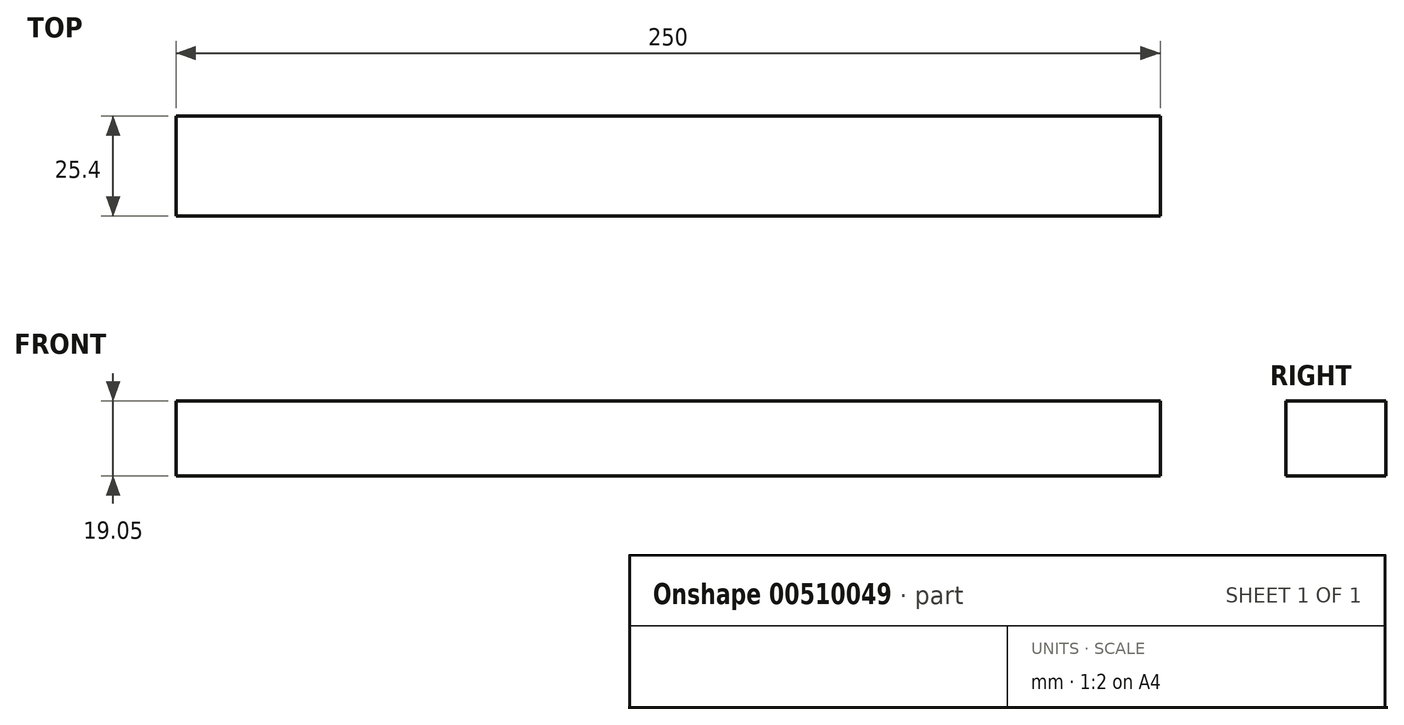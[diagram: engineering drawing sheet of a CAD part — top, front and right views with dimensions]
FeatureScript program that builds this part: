
annotation { "Feature Type Name" : "Feature", "Feature Type Description" : "" }
export const myFeature = defineFeature(function(context is Context, id is Id, definition is map)
    precondition{}
    {
        {
            var Q0;
            Q0=qCreatedBy(makeId("Front.planeOp"),FACE);
            var sketch = newSketch(context, id + "F0", { "sketchPlane" : qUnion([Q0])});
            skLineSegment(sketch, "E0.bottom", {"start": v(-138.16, -1.41) * mm, "end": v(111.84, -1.41) * mm});
            skLineSegment(sketch, "E0.top", {"start": v(-138.16, -20.46) * mm, "end": v(111.84, -20.46) * mm});
            skLineSegment(sketch, "E0.left", {"start": v(-138.16, -1.41) * mm, "end": v(-138.16, -20.46) * mm});
            skLineSegment(sketch, "E0.right", {"start": v(111.84, -1.41) * mm, "end": v(111.84, -20.46) * mm});
            skSolve(sketch);
        }
        {
            var Q0;
            Q0=qSketchRegion(id+"F0",true);
            extrude(context, id + "F1", {"entities" : qUnion([Q0]), "depth" : 25.4 * mm});
        }
    });
